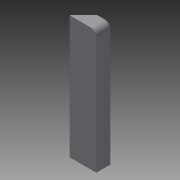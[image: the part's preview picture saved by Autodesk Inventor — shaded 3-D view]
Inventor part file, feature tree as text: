
AUTODESK INVENTOR PART (.ipt)
format: ipt  version: 2015 (Build 190159000, 159)  size: 76,800 bytes
history: native  units: mm
features: extrude x1, fillet x1, chamfer x1, sketch x1
ambient origin geometry x8: Origin, YZ Plane, XZ Plane, XY Plane, X Axis, Y Axis, Z Axis, Center Point
bodies: Solid1 (feature_tree)
feature tree (4):
  extrude  "Extrusion1"  Depth=88.0mm
  fillet  "Fillet1"  Radius=10.0mm
  chamfer  "Chamfer1"  Distance=4.0mm
  sketch  "Sketch1"  dims[d0=19.0mm d1=88.0mm d2=10.0mm d3=0.0mm d4=4.0mm d5=9.5mm d6=2.0mm d7=45.0deg]
